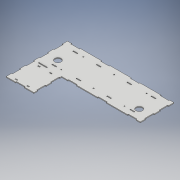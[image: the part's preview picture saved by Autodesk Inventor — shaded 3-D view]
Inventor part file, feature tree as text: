
AUTODESK INVENTOR PART (.ipt)
format: ipt  version: 2018 (Build 220112000, 112)  size: 479,744 bytes
history: native  units: mm
features: extrude x8, sketch x7, other x3, projected_geometry x3, plane x2, mirror x2
ambient origin geometry x8: Origin, YZ Plane, XZ Plane, XY Plane, X Axis, Y Axis, Z Axis, Center Point
bodies: Solid1 (feature_tree)
feature tree (25):
  other  "Table"
  other  "FLOOR-01"
  other  "FLOOR-02"
  extrude  "Extrusion1"  Depth=4.0mm TaperAngle=0.0deg
  extrude  "Extrusion2"  Depth=4.0mm
  plane  "Work Plane1"
  mirror  "Mirror1"
  extrude  "Extrusion3"  Depth=4.0mm
  plane  "Work Plane2"
  mirror  "Mirror2"
  extrude  "Extrusion5"  Depth=39.8mm
  sketch  "Sketch8"  dims[d9=4.0mm d10=20.0mm]
  extrude  "Extrusion6"  Depth=20.0mm
  extrude  "Extrusion7"  Depth=378.4mm
  extrude  "Extrusion8"  Depth=39.8mm
  extrude  "Extrusion9"  Depth=4.0mm
  sketch  "Sketch1"  dims[d0=25.0mm d1=4.0mm d2=0.0mm]
  sketch  "Sketch2"  dims[d3=39.8mm d4=4.0mm]
  projected_geometry  "Projected Loop1"
  sketch  "Sketch3"  dims[d5=39.8mm d6=4.0mm]
  projected_geometry  "Projected Loop2"
  sketch  "Sketch7"  dims[d7=39.8mm d8=39.8mm]
  projected_geometry  "Projected Loop4"
  sketch  "Sketch10"  dims[d11=20.0mm d12=378.4mm]
  sketch  "Sketch11"  dims[d16=4.0mm d17=0.0mm d18=39.8mm d19=4.0mm d20=39.8mm d21=4.0mm d22=157.2mm d25=4.0mm d26=0.0mm d31=130.0mm d32=130.0mm d33=4.0mm d34=0.0mm d35=4.0mm d36=39.8mm d37=25.0mm d38=4.0mm d39=39.8mm d41=4.0mm d42=0.0mm d51=4.0mm d52=39.8mm d53=4.0mm d54=39.8mm d55=39.8mm d56=4.0mm d57=4.0mm d58=0.0mm d59=30.0mm d60=50.0mm d61=55.0mm d62=30.0mm d63=100.0mm d64=55.0mm d65=4.0mm d66=0.0mm d67=10.0mm d68=0.0mm]
